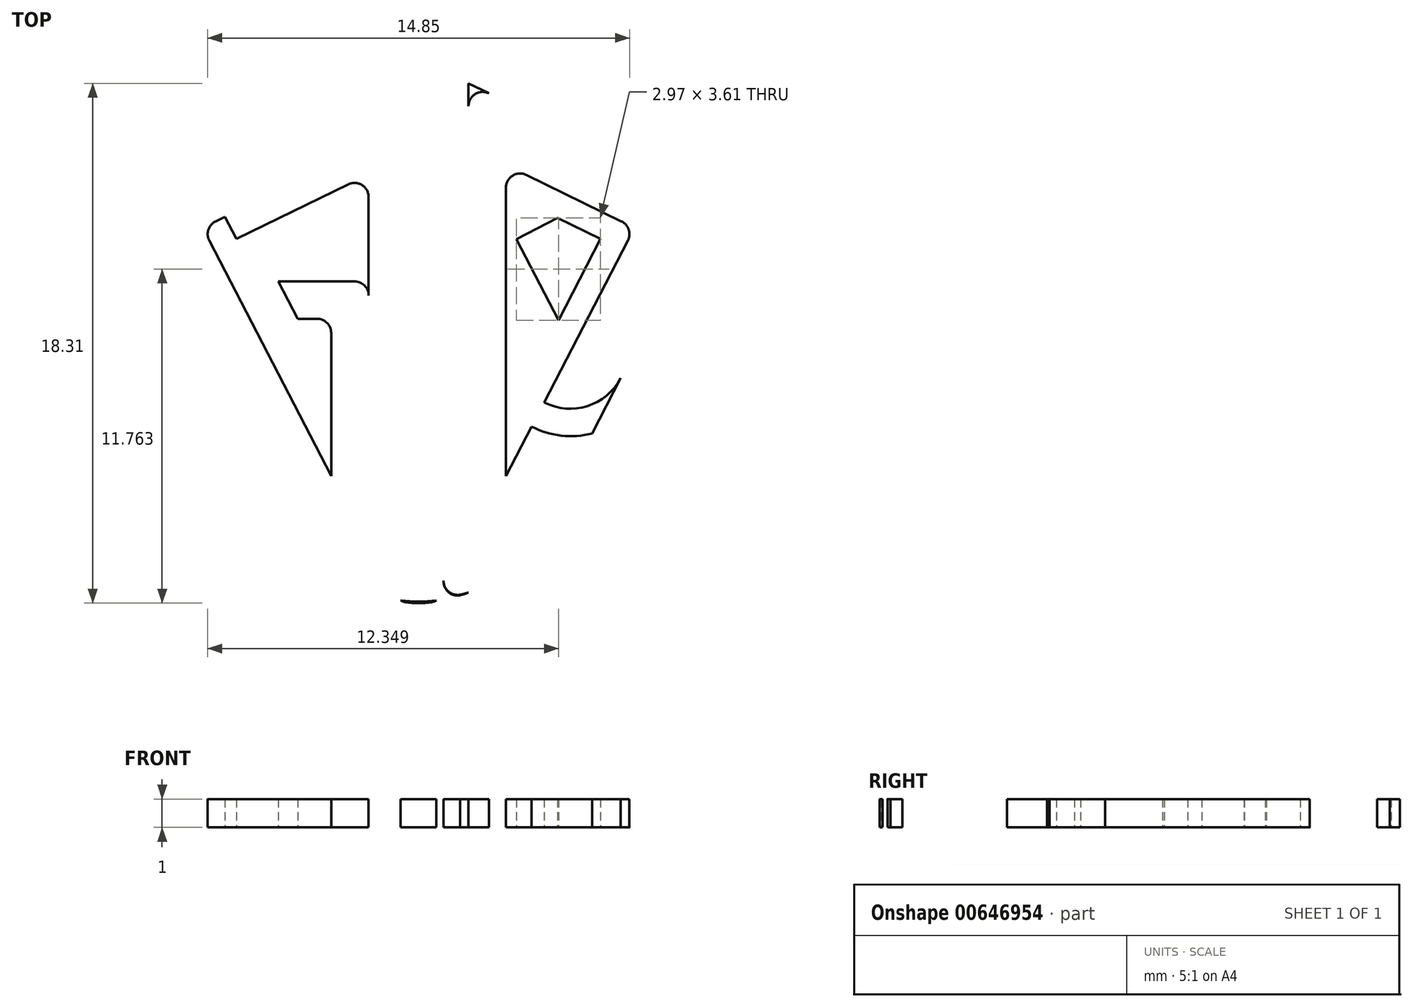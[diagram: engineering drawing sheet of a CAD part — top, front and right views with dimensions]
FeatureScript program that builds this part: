
annotation { "Feature Type Name" : "Feature", "Feature Type Description" : "" }
export const myFeature = defineFeature(function(context is Context, id is Id, definition is map)
    precondition{}
    {
        {
            var Q0;
            Q0=qCreatedBy(makeId("Top.planeOp"),FACE);
            var sketch = newSketch(context, id + "F0", { "sketchPlane" : qUnion([Q0])});
            skArc(sketch, "E0.MirrorCS", {"start": v(-12.62, 8.93) * mm, "mid": v(-12.18, 9.03) * mm, "end": v(-11.74, 8.93) * mm});
            skArc(sketch, "E1.MirrorCS", {"start": v(-1.42, 3.88) * mm, "mid": v(-0.9, 3.3) * mm, "end": v(-0.97, 2.52) * mm});
            skArc(sketch, "E2.MirrorCS", {"start": v(-23.38, 2.52) * mm, "mid": v(-23.45, 3.3) * mm, "end": v(-22.94, 3.88) * mm});
            skPoint(sketch, "E3.MirrorP", {"position": v(-23.85, 3.43) * mm});
            skArc(sketch, "E4.MirrorCS", {"start": v(-6.85, -8.84) * mm, "mid": v(-12.18, -12.09) * mm, "end": v(-17.5, -8.84) * mm});
            skLineSegment(sketch, "E5.MirrorCS", {"start": v(-4.15, -3.64) * mm, "end": v(-0.97, 2.52) * mm});
            skLineSegment(sketch, "E6.MirrorCS", {"start": v(-12.62, 8.93) * mm, "end": v(-22.94, 3.88) * mm});
            skLineSegment(sketch, "E7.MirrorCS", {"start": v(-23.38, 2.52) * mm, "end": v(-17.5, -8.84) * mm});
            skLineSegment(sketch, "E8.MirrorCS", {"start": v(-1.42, 3.88) * mm, "end": v(-11.74, 8.93) * mm});
            skLineSegment(sketch, "E9", {"start": v(-22.26, 2.53) * mm, "end": v(-16.62, -8.38) * mm});
            skArc(sketch, "E10.filletArc", {"start": v(-9.67, -10.41) * mm, "mid": v(-8.56, -9.53) * mm, "end": v(-7.74, -8.38) * mm});
            skLineSegment(sketch, "E11.MirrorCS", {"start": v(-10.42, 3.03) * mm, "end": v(-10.42, 0.52) * mm});
            skLineSegment(sketch, "E12.bottom", {"start": v(-15.25, 0.2) * mm, "end": v(-16.07, 0.2) * mm});
            skLineSegment(sketch, "E12.top", {"start": v(-15.75, -1.12) * mm, "end": v(-16.07, -1.12) * mm});
            skLineSegment(sketch, "E13", {"start": v(-15.25, 0.2) * mm, "end": v(-14.44, 0.2) * mm});
            skPoint(sketch, "E14", {"position": v(-16.57, -8.47) * mm});
            skPoint(sketch, "E15", {"position": v(-15.25, -10.03) * mm});
            skPoint(sketch, "E16", {"position": v(-13.94, -10.77) * mm});
            skPoint(sketch, "E17", {"position": v(-13.06, -11) * mm});
            skPoint(sketch, "E18", {"position": v(-11.3, -11) * mm});
            skPoint(sketch, "E19", {"position": v(-10.42, -10.77) * mm});
            skPoint(sketch, "E20", {"position": v(-9.1, -10.03) * mm});
            skPoint(sketch, "E21", {"position": v(-9.1, -6.67) * mm});
            skPoint(sketch, "E22", {"position": v(-2.78, 1.2) * mm});
            skPoint(sketch, "E23", {"position": v(-4.57, 2.08) * mm});
            skPoint(sketch, "E24", {"position": v(-9.1, 6.52) * mm});
            skPoint(sketch, "E25", {"position": v(-10.42, 7.17) * mm});
            skPoint(sketch, "E26", {"position": v(-11.3, 7.6) * mm});
            skPoint(sketch, "E27", {"position": v(-13.06, 7.6) * mm});
            skPoint(sketch, "E28", {"position": v(-13.94, 7.17) * mm});
            skPoint(sketch, "E29", {"position": v(-15.25, 4.3) * mm});
            skPoint(sketch, "E30", {"position": v(-13.94, 4.94) * mm});
            skPoint(sketch, "E31", {"position": v(-13.06, 5.37) * mm});
            skPoint(sketch, "E32", {"position": v(-10.42, 4.94) * mm});
            skPoint(sketch, "E33", {"position": v(-21.58, 1.2) * mm});
            skPoint(sketch, "E34", {"position": v(-19.78, 2.08) * mm});
            skPoint(sketch, "E35", {"position": v(-16.57, -4.12) * mm});
            skPoint(sketch, "E36", {"position": v(-16.57, -1.12) * mm});
            skPoint(sketch, "E37", {"position": v(-16.57, 0.2) * mm});
            skPoint(sketch, "E38", {"position": v(-15.25, 0.2) * mm});
            skPoint(sketch, "E39", {"position": v(-15.25, -1.12) * mm});
            skPoint(sketch, "E40", {"position": v(-13.94, 0.2) * mm});
            skLineSegment(sketch, "E41", {"start": v(-2.78, 1.2) * mm, "end": v(-2.1, 2.53) * mm});
            skLineSegment(sketch, "E42", {"start": v(-3.82, 3.94) * mm, "end": v(-6.39, 5.2) * mm});
            skLineSegment(sketch, "E43", {"start": v(-6.4, -1.43) * mm, "end": v(-4.8, 1.63) * mm});
            skLineSegment(sketch, "E44", {"start": v(-5.03, 2.3) * mm, "end": v(-6.4, 2.97) * mm});
            skLineSegment(sketch, "E45", {"start": v(-9.1, 3.5) * mm, "end": v(-9.1, -6.67) * mm});
            skLineSegment(sketch, "E46", {"start": v(-22.04, 3.2) * mm, "end": v(-14.65, 6.82) * mm});
            skLineSegment(sketch, "E47", {"start": v(-12.78, 7.74) * mm, "end": v(-12.4, 7.92) * mm});
            skLineSegment(sketch, "E48", {"start": v(-11.96, 7.92) * mm, "end": v(-11.58, 7.74) * mm});
            skLineSegment(sketch, "E49", {"start": v(-15.25, 4.3) * mm, "end": v(-19.32, 2.3) * mm});
            skLineSegment(sketch, "E50", {"start": v(-19.55, 1.63) * mm, "end": v(-16.57, -4.12) * mm});
            skLineSegment(sketch, "E51", {"start": v(-15.25, -1.62) * mm, "end": v(-15.25, -10.03) * mm});
            skPoint(sketch, "E52", {"position": v(-15.25, -6.67) * mm});
            skLineSegment(sketch, "E53", {"start": v(-16.57, -4.12) * mm, "end": v(-15.25, -6.67) * mm});
            skLineSegment(sketch, "E54", {"start": v(-15.25, 4.3) * mm, "end": v(-14.65, 4.59) * mm});
            skLineSegment(sketch, "E55", {"start": v(-9.1, 6.52) * mm, "end": v(-9.7, 6.82) * mm});
            skArc(sketch, "E56.filletArc", {"start": v(-22.04, 3.2) * mm, "mid": v(-22.3, 2.91) * mm, "end": v(-22.26, 2.53) * mm});
            skArc(sketch, "E57.filletArc", {"start": v(-2.1, 2.53) * mm, "mid": v(-2.06, 2.91) * mm, "end": v(-2.32, 3.2) * mm});
            skArc(sketch, "E58.filletArc", {"start": v(-13.94, 6.37) * mm, "mid": v(-14.17, 6.8) * mm, "end": v(-14.65, 6.82) * mm});
            skArc(sketch, "E59.filletArc", {"start": v(-9.7, 6.82) * mm, "mid": v(-10.18, 6.8) * mm, "end": v(-10.42, 6.37) * mm});
            skArc(sketch, "E60.filletArc", {"start": v(-8.38, 3.94) * mm, "mid": v(-8.87, 3.92) * mm, "end": v(-9.1, 3.5) * mm});
            skArc(sketch, "E61.filletArc", {"start": v(-4.8, 1.63) * mm, "mid": v(-4.78, 2.01) * mm, "end": v(-5.03, 2.3) * mm});
            skArc(sketch, "E62.filletArc", {"start": v(-19.32, 2.3) * mm, "mid": v(-19.58, 2.01) * mm, "end": v(-19.55, 1.63) * mm});
            skArc(sketch, "E63.filletArc", {"start": v(-13.94, 4.14) * mm, "mid": v(-14.17, 4.56) * mm, "end": v(-14.65, 4.59) * mm});
            skArc(sketch, "E64.filletArc", {"start": v(-15.25, -1.62) * mm, "mid": v(-15.4, -1.27) * mm, "end": v(-15.75, -1.12) * mm});
            skArc(sketch, "E65.filletArc", {"start": v(-13.94, -0.3) * mm, "mid": v(-14.08, 0.05) * mm, "end": v(-14.44, 0.2) * mm});
            skLineSegment(sketch, "E66", {"start": v(-13.94, 4.14) * mm, "end": v(-13.94, 6.37) * mm});
            skArc(sketch, "E67.filletArc", {"start": v(-11.96, 7.92) * mm, "mid": v(-12.18, 7.97) * mm, "end": v(-12.4, 7.92) * mm});
            skArc(sketch, "E68.filletArc", {"start": v(-12.78, 7.74) * mm, "mid": v(-12.98, 7.55) * mm, "end": v(-13.06, 7.29) * mm});
            skArc(sketch, "E69.filletArc", {"start": v(-11.3, 7.29) * mm, "mid": v(-11.37, 7.55) * mm, "end": v(-11.58, 7.74) * mm});
            skArc(sketch, "E70.filletArc", {"start": v(-10.42, -9.98) * mm, "mid": v(-10.17, -10.41) * mm, "end": v(-9.67, -10.41) * mm});
            skArc(sketch, "E71.MirrorCS", {"start": v(-14.69, -10.41) * mm, "mid": v(-15.8, -9.53) * mm, "end": v(-16.62, -8.38) * mm});
            skArc(sketch, "E72.MirrorCS", {"start": v(-13.94, -9.98) * mm, "mid": v(-14.19, -10.41) * mm, "end": v(-14.69, -10.41) * mm});
            skArc(sketch, "E73", {"start": v(-12.63, -11.1) * mm, "mid": v(-12.18, -11.14) * mm, "end": v(-11.72, -11.1) * mm});
            skLineSegment(sketch, "E74", {"start": v(-13.94, -9.98) * mm, "end": v(-13.94, -0.3) * mm});
            skLineSegment(sketch, "E75", {"start": v(-13.06, -10.37) * mm, "end": v(-13.06, 6.8) * mm});
            skLineSegment(sketch, "E76", {"start": v(-11.3, 7.29) * mm, "end": v(-11.3, -10.35) * mm});
            skArc(sketch, "E77.filletArc", {"start": v(-13.06, -10.61) * mm, "mid": v(-12.94, -10.94) * mm, "end": v(-12.63, -11.1) * mm});
            skArc(sketch, "E78.filletArc", {"start": v(-11.72, -11.1) * mm, "mid": v(-11.42, -10.94) * mm, "end": v(-11.3, -10.61) * mm});
            skLineSegment(sketch, "E79", {"start": v(-16.07, 0.2) * mm, "end": v(-17.12, 0.2) * mm});
            skLineSegment(sketch, "E80", {"start": v(-16.07, -1.12) * mm, "end": v(-16.57, -1.12) * mm});
            skPoint(sketch, "E81", {"position": v(-16.43, -1.12) * mm});
            skLineSegment(sketch, "E82", {"start": v(-16.43, -1.12) * mm, "end": v(-17.12, 0.2) * mm});
            skPoint(sketch, "E83", {"position": v(-6.84, 2.08) * mm});
            skPoint(sketch, "E84", {"position": v(-6.84, 3.19) * mm});
            skPoint(sketch, "E85", {"position": v(-6.84, -2.3) * mm});
            skPoint(sketch, "E86", {"position": v(-9.1, 2.08) * mm});
            skLineSegment(sketch, "E87", {"start": v(-7.28, 2.97) * mm, "end": v(-8.64, 2.3) * mm});
            skLineSegment(sketch, "E88", {"start": v(-8.87, 1.63) * mm, "end": v(-7.28, -1.43) * mm});
            skPoint(sketch, "E89", {"position": v(-6.83, 5.4) * mm});
            skPoint(sketch, "E90", {"position": v(-5.42, 0.45) * mm});
            skPoint(sketch, "E91", {"position": v(-10.42, 3.65) * mm});
            skLineSegment(sketch, "E92", {"start": v(-9.86, 3.93) * mm, "end": v(-7.27, 5.2) * mm});
            skPoint(sketch, "E93", {"position": v(-7.96, -4.47) * mm});
            skPoint(sketch, "E94", {"position": v(-10.42, 0.28) * mm});
            skPoint(sketch, "E95", {"position": v(-9.1, -2.27) * mm});
            skLineSegment(sketch, "E96", {"start": v(-6.84, 3.19) * mm, "end": v(-6.84, 2.08) * mm});
            skPoint(sketch, "E97", {"position": v(-3.26, 0.28) * mm});
            skPoint(sketch, "E98", {"position": v(-3.26, 3.66) * mm});
            skLineSegment(sketch, "E99", {"start": v(-3.26, 3.04) * mm, "end": v(-3.26, 0.52) * mm});
            skLineSegment(sketch, "E100", {"start": v(-12.18, -6.09) * mm, "end": v(-12.18, -8.2) * mm});
            skLineSegment(sketch, "E101.MirrorCS", {"start": v(-21.1, 3.66) * mm, "end": v(-21.1, 0.28) * mm});
            skLineSegment(sketch, "E102.MirrorCS", {"start": v(-4.57, 2.08) * mm, "end": v(-6.84, -2.3) * mm});
            skLineSegment(sketch, "E103.MirrorCS", {"start": v(-6.84, 3.19) * mm, "end": v(-4.57, 2.08) * mm});
            skPoint(sketch, "E104", {"position": v(-11.3, 5.38) * mm});
            skPoint(sketch, "E105", {"position": v(-11.3, -10.04) * mm});
            skPoint(sketch, "E106", {"position": v(-13.06, -10.04) * mm});
            skPoint(sketch, "E107", {"position": v(-12.17, 5.8) * mm});
            skPoint(sketch, "E108", {"position": v(-13.06, -6.65) * mm});
            skPoint(sketch, "E109", {"position": v(-11.3, -6.65) * mm});
            skLineSegment(sketch, "E110", {"start": v(-13.94, 7.17) * mm, "end": v(-13.78, 7.25) * mm});
            skLineSegment(sketch, "E111", {"start": v(-13.06, 5.37) * mm, "end": v(-13.06, 7.6) * mm});
            skArc(sketch, "E112.filletArc", {"start": v(-13.06, 6.8) * mm, "mid": v(-13.3, 7.22) * mm, "end": v(-13.78, 7.25) * mm});
            skLineSegment(sketch, "E113", {"start": v(-13.94, 7.17) * mm, "end": v(-12.78, 7.74) * mm});
            skLineSegment(sketch, "E114", {"start": v(-11.3, -10.04) * mm, "end": v(-11.3, -11) * mm});
            skLineSegment(sketch, "E115", {"start": v(-10.42, -10.77) * mm, "end": v(-10.67, -10.83) * mm});
            skArc(sketch, "E116.filletArc", {"start": v(-11.3, -10.35) * mm, "mid": v(-11.1, -10.75) * mm, "end": v(-10.67, -10.83) * mm});
            skLineSegment(sketch, "E117", {"start": v(-13.06, -10.04) * mm, "end": v(-13.06, -11) * mm});
            skLineSegment(sketch, "E118", {"start": v(-14.06, -10.77) * mm, "end": v(-13.67, -10.86) * mm});
            skPoint(sketch, "E119.newPointA", {"position": v(-13.06, -10.61) * mm});
            skArc(sketch, "E119.filletArc", {"start": v(-13.67, -10.86) * mm, "mid": v(-13.25, -10.77) * mm, "end": v(-13.06, -10.37) * mm});
            skLineSegment(sketch, "E120", {"start": v(-21.58, 1.2) * mm, "end": v(-16.62, -8.38) * mm});
            skPoint(sketch, "E121", {"position": v(-12.18, -16.97) * mm});
            skArc(sketch, "E122.filletArc", {"start": v(-16.62, -8.38) * mm, "mid": v(-12.18, -11.09) * mm, "end": v(-7.74, -8.38) * mm});
            skArc(sketch, "E123.filletArc", {"start": v(-6.39, 5.2) * mm, "mid": v(-6.83, 5.3) * mm, "end": v(-7.27, 5.2) * mm});
            skArc(sketch, "E124.filletArc", {"start": v(-3.26, 3.04) * mm, "mid": v(-3.4, 3.57) * mm, "end": v(-3.82, 3.94) * mm});
            skArc(sketch, "E125.filletArc", {"start": v(-3.37, 0.06) * mm, "mid": v(-3.28, 0.28) * mm, "end": v(-3.26, 0.52) * mm});
            skArc(sketch, "E126.filletArc", {"start": v(-9.86, 3.93) * mm, "mid": v(-10.27, 3.56) * mm, "end": v(-10.42, 3.03) * mm});
            skArc(sketch, "E127.filletArc", {"start": v(-10.42, 0.52) * mm, "mid": v(-10.4, 0.28) * mm, "end": v(-10.3, 0.06) * mm});
            skArc(sketch, "E128.filletArc", {"start": v(-6.4, 2.97) * mm, "mid": v(-6.84, 3.08) * mm, "end": v(-7.28, 2.97) * mm});
            skArc(sketch, "E129.filletArc", {"start": v(-8.64, 2.3) * mm, "mid": v(-8.9, 2.01) * mm, "end": v(-8.87, 1.63) * mm});
            skLineSegment(sketch, "E130", {"start": v(-3.82, 3.94) * mm, "end": v(-11.3, 7.6) * mm});
            skLineSegment(sketch, "E131", {"start": v(-10.42, 0.52) * mm, "end": v(-10.42, 7.17) * mm});
            skLineSegment(sketch, "E132", {"start": v(-9.77, 4.95) * mm, "end": v(-7.83, 5.9) * mm});
            skLineSegment(sketch, "E133", {"start": v(-7.83, 5.9) * mm, "end": v(-9.77, 4.95) * mm});
            skLineSegment(sketch, "E134", {"start": v(-9.77, 4.95) * mm, "end": v(-10.42, 4.63) * mm});
            skPoint(sketch, "E135", {"position": v(-8.5, -3.42) * mm});
            skLineSegment(sketch, "E136", {"start": v(-16.9, 2.51) * mm, "end": v(-19.8, 1.1) * mm});
            skLineSegment(sketch, "E137", {"start": v(-19.8, 1.1) * mm, "end": v(-16.9, 2.51) * mm});
            skLineSegment(sketch, "E138", {"start": v(-16.9, 2.51) * mm, "end": v(-14.65, 3.61) * mm});
            skLineSegment(sketch, "E139", {"start": v(-19.12, 0.8) * mm, "end": v(-18.34, 1.21) * mm});
            skLineSegment(sketch, "E140", {"start": v(-18.34, 1.21) * mm, "end": v(-19.55, 3.55) * mm});
            skLineSegment(sketch, "E141", {"start": v(-19.55, 3.55) * mm, "end": v(-18.34, 1.21) * mm});
            skLineSegment(sketch, "E142", {"start": v(-19.55, 3.55) * mm, "end": v(-15.64, -4.01) * mm});
            skLineSegment(sketch, "E143", {"start": v(-16.13, -2.63) * mm, "end": v(-16.13, -3.81) * mm});
            skLineSegment(sketch, "E144", {"start": v(-16.13, -1.46) * mm, "end": v(-16.13, -3.81) * mm});
            skLineSegment(sketch, "E145", {"start": v(-13.94, 3.16) * mm, "end": v(-13.94, -0.3) * mm});
            skLineSegment(sketch, "E146", {"start": v(-15.25, 1.07) * mm, "end": v(-18.6, 1.07) * mm});
            skLineSegment(sketch, "E147", {"start": v(-18.6, 1.07) * mm, "end": v(-15.25, 1.07) * mm});
            skLineSegment(sketch, "E148", {"start": v(-13.7, 1.07) * mm, "end": v(-15.25, 1.07) * mm});
            skArc(sketch, "E149.filletArc", {"start": v(-13.94, 3.16) * mm, "mid": v(-14.17, 3.59) * mm, "end": v(-14.65, 3.61) * mm});
            skLineSegment(sketch, "E150", {"start": v(-2.38, 2.4) * mm, "end": v(-2.38, 1.75) * mm});
            skLineSegment(sketch, "E151", {"start": v(-2.38, 1.75) * mm, "end": v(-2.38, 3.6) * mm});
            skLineSegment(sketch, "E152", {"start": v(-3.82, 3.94) * mm, "end": v(-1.86, 2.98) * mm});
            skLineSegment(sketch, "E153", {"start": v(-16.07, -2) * mm, "end": v(-17.03, -2) * mm});
            skArc(sketch, "E154.filletArc", {"start": v(-7.28, -1.43) * mm, "mid": v(-6.84, -1.7) * mm, "end": v(-6.4, -1.43) * mm});
            skLineSegment(sketch, "E155", {"start": v(-7.74, -8.38) * mm, "end": v(-6.84, -6.65) * mm});
            skPoint(sketch, "E156", {"position": v(-7.9, 1.68) * mm});
            skPoint(sketch, "E157", {"position": v(-6.86, 2.22) * mm});
            skPoint(sketch, "E158", {"position": v(-5.77, 1.69) * mm});
            skPoint(sketch, "E159", {"position": v(-6.84, -0.38) * mm});
            skLineSegment(sketch, "E160", {"start": v(-7.9, 1.68) * mm, "end": v(-6.86, 2.22) * mm});
            skLineSegment(sketch, "E161", {"start": v(-6.86, 2.22) * mm, "end": v(-5.77, 1.69) * mm});
            skLineSegment(sketch, "E162", {"start": v(-5.77, 1.69) * mm, "end": v(-6.84, -0.38) * mm});
            skLineSegment(sketch, "E163", {"start": v(-6.84, -0.38) * mm, "end": v(-7.9, 1.68) * mm});
            skLineSegment(sketch, "E164.MirrorCS", {"start": v(-10.42, -9.98) * mm, "end": v(-10.42, -0.3) * mm});
            skPoint(sketch, "E165", {"position": v(-6.82, -8.79) * mm});
            skLineSegment(sketch, "E166", {"start": v(-6.85, -8.84) * mm, "end": v(-6.82, -8.79) * mm});
            skPoint(sketch, "E167", {"position": v(-6.84, -6.65) * mm});
            skLineSegment(sketch, "E168", {"start": v(-2.78, 1.2) * mm, "end": v(-5.06, -3.21) * mm});
            skLineSegment(sketch, "E169", {"start": v(-8.61, -3.21) * mm, "end": v(-10.42, 0.28) * mm});
            skLineSegment(sketch, "E170", {"start": v(-10.42, 0.52) * mm, "end": v(-10.42, -0.3) * mm});
            skArc(sketch, "E171.filletArc", {"start": v(-8.61, -3.21) * mm, "mid": v(-6.84, -4.3) * mm, "end": v(-5.06, -3.21) * mm});
            skPoint(sketch, "E172", {"position": v(-10.42, -1.83) * mm});
            skPoint(sketch, "E173", {"position": v(-9.1, -4.38) * mm});
            skLineSegment(sketch, "E174", {"start": v(-5.5, -4.07) * mm, "end": v(-5.06, -3.21) * mm});
            skLineSegment(sketch, "E175", {"start": v(-9.1, -2.27) * mm, "end": v(-8.17, -4.07) * mm});
            skPoint(sketch, "E176", {"position": v(-0.97, 2.52) * mm});
            skPoint(sketch, "E177", {"position": v(-4.15, -3.64) * mm});
            skLineSegment(sketch, "E178", {"start": v(-10.42, -1.83) * mm, "end": v(-9.48, -3.64) * mm});
            skArc(sketch, "E179.filletArc", {"start": v(-9.48, -3.64) * mm, "mid": v(-6.82, -5.26) * mm, "end": v(-4.15, -3.64) * mm});
            skLineSegment(sketch, "E180", {"start": v(-6.82, -8.79) * mm, "end": v(-4.15, -3.64) * mm});
            skLineSegment(sketch, "E181", {"start": v(-6.84, -6.65) * mm, "end": v(-3.26, 0.28) * mm});
            skArc(sketch, "E182.MirrorCS", {"start": v(-10.68, -10.86) * mm, "mid": v(-11.1, -10.77) * mm, "end": v(-11.3, -10.37) * mm});
            skArc(sketch, "E183.MirrorCS", {"start": v(-11.3, -10.61) * mm, "mid": v(-11.42, -10.94) * mm, "end": v(-11.72, -11.1) * mm});
            skArc(sketch, "E184.MirrorCS", {"start": v(-7.74, -8.38) * mm, "mid": v(-12.18, -11.09) * mm, "end": v(-16.62, -8.38) * mm});
            skLineSegment(sketch, "E185.MirrorCS", {"start": v(-4.8, 1.63) * mm, "end": v(-7.78, -4.12) * mm});
            skLineSegment(sketch, "E186.MirrorCS", {"start": v(-9.1, -1.62) * mm, "end": v(-9.1, -10.03) * mm});
            skLineSegment(sketch, "E187.MirrorCS", {"start": v(-9.1, 4.3) * mm, "end": v(-5.03, 2.3) * mm});
            skArc(sketch, "E188.MirrorCS", {"start": v(-5.03, 2.3) * mm, "mid": v(-4.78, 2.01) * mm, "end": v(-4.8, 1.63) * mm});
            skLineSegment(sketch, "E189.MirrorCS", {"start": v(-7.78, -4.12) * mm, "end": v(-9.1, -6.67) * mm});
            skLineSegment(sketch, "E190", {"start": v(-5.77, 1.69) * mm, "end": v(-4.78, 1.69) * mm});
            skLineSegment(sketch, "E191", {"start": v(-7.9, 1.68) * mm, "end": v(-9.1, 1.68) * mm});
            skLineSegment(sketch, "E192", {"start": v(-9.1, 1.68) * mm, "end": v(-8.11, 1.68) * mm});
            skLineSegment(sketch, "E193", {"start": v(-8.11, 1.68) * mm, "end": v(-9.1, 1.68) * mm});
            skPoint(sketch, "E194", {"position": v(-8.11, 1.68) * mm});
            skLineSegment(sketch, "E195", {"start": v(-8.11, 1.68) * mm, "end": v(-6.61, 2.46) * mm});
            skLineSegment(sketch, "E196", {"start": v(-5.77, 1.69) * mm, "end": v(-7.06, 2.32) * mm});
            skPoint(sketch, "E197", {"position": v(-6.97, 2.27) * mm});
            skLineSegment(sketch, "E198", {"start": v(-8.11, 1.68) * mm, "end": v(-6.76, -0.93) * mm});
            skLineSegment(sketch, "E199", {"start": v(-5.77, 1.69) * mm, "end": v(-7.05, -0.78) * mm});
            skPoint(sketch, "E200", {"position": v(-6.94, -0.58) * mm});
            skLineSegment(sketch, "E201.MirrorCS", {"start": v(-7.17, -0.55) * mm, "end": v(-8.23, 1.51) * mm});
            skLineSegment(sketch, "E202.MirrorCS", {"start": v(-8, 1.85) * mm, "end": v(-6.95, 2.4) * mm});
            skLineSegment(sketch, "E203", {"start": v(-8, 1.85) * mm, "end": v(-8.6, 1.55) * mm});
            skLineSegment(sketch, "E204", {"start": v(-8.23, 1.51) * mm, "end": v(-8.46, 1.98) * mm});
            skLineSegment(sketch, "E205", {"start": v(-7.17, -0.55) * mm, "end": v(-6.89, -1.08) * mm});
            skLineSegment(sketch, "E206", {"start": v(-7.06, 2.32) * mm, "end": v(-7.16, 2.37) * mm});
            skLineSegment(sketch, "E207.MirrorCS", {"start": v(-8.2, 1.85) * mm, "end": v(-6.7, 2.62) * mm});
            skLineSegment(sketch, "E208.MirrorCS", {"start": v(-8.08, 2.02) * mm, "end": v(-7.03, 2.56) * mm});
            skLineSegment(sketch, "E209.MirrorCS", {"start": v(-8.44, 1.51) * mm, "end": v(-7.09, -1.1) * mm});
            skLineSegment(sketch, "E210.MirrorCS", {"start": v(-7.5, -0.72) * mm, "end": v(-8.56, 1.34) * mm});
            skLineSegment(sketch, "E211", {"start": v(-6.84, -0.38) * mm, "end": v(-7.28, -1.24) * mm});
            skLineSegment(sketch, "E212", {"start": v(-7.5, -0.72) * mm, "end": v(-7.18, -1.33) * mm});
            skLineSegment(sketch, "E213", {"start": v(-8.2, 1.85) * mm, "end": v(-8.7, 1.6) * mm});
            skLineSegment(sketch, "E214", {"start": v(-8.08, 2.02) * mm, "end": v(-8.8, 1.65) * mm});
            skLineSegment(sketch, "E215", {"start": v(-8.56, 1.34) * mm, "end": v(-8.77, 1.75) * mm});
            skLineSegment(sketch, "E216", {"start": v(-8.44, 1.51) * mm, "end": v(-8.6, 1.85) * mm});
            skPoint(sketch, "E216.endSnap0", {"position": v(-8.6, 1.68) * mm});
            skLineSegment(sketch, "E217", {"start": v(-8.6, 1.55) * mm, "end": v(-8.72, 1.49) * mm});
            skLineSegment(sketch, "E218", {"start": v(-7.16, 2.37) * mm, "end": v(-7.76, 2.66) * mm});
            skLineSegment(sketch, "E219.MirrorCS", {"start": v(-2.78, 1.2) * mm, "end": v(-7.74, -8.38) * mm});
            skLineSegment(sketch, "E220.MirrorCS", {"start": v(-0.97, 2.52) * mm, "end": v(-6.85, -8.84) * mm});
            skPoint(sketch, "E221.newPointA", {"position": v(-10.7, -19.84) * mm});
            skPoint(sketch, "E221.newPointB", {"position": v(-13.66, -19.84) * mm});
            skPoint(sketch, "E222.newPointA", {"position": v(-10.27, -22.82) * mm});
            skPoint(sketch, "E222.newPointB", {"position": v(-14.08, -22.82) * mm});
            skArc(sketch, "E222.filletArc", {"start": v(-17.5, -8.84) * mm, "mid": v(-12.18, -12.09) * mm, "end": v(-6.85, -8.84) * mm});
            skSolve(sketch);
        }
        {
            var Q0;
            {var subQ4=sQuery(id+"F0.wireOp",EDGE,"E138");Q0=makeQuery(id+"F0.imprint","IMPRINT",FACE,{"disambiguationData":[TD([[makeQuery(id+"F0.imprint","IMPRINT",EDGE,{"derivedFrom":subQ4}),-1.0]])]});}
            var Q1;
            Q1=makeQuery(id+"F0.imprint","IMPRINT",FACE,{"disambiguationData":[TD([[makeQuery(id+"F0.imprint","IMPRINT",EDGE,{"derivedFrom":sQuery(id+"F0.wireOp",EDGE,"E12.bottom")}),-1.0]])]});
            var Q2;
            {var subQ0=sQuery(id+"F0.wireOp",EDGE,"E144");var subQ5=makeQuery(id+"F0.imprint","IMPRINT",VERTEX,{"derivedFrom":subQ0});Q2=makeQuery(id+"F0.imprint","IMPRINT",FACE,{"disambiguationData":[TD([[makeQuery(id+"F0.imprint","IMPRINT",EDGE,{"disambiguationData":[TD([[subQ5,1.0]])],"derivedFrom":subQ0}),-1.0]])]});}
            var Q3;
            {var subQ0=sQuery(id+"F0.wireOp",EDGE,"E62.filletArc");Q3=makeQuery(id+"F0.imprint","IMPRINT",FACE,{"disambiguationData":[TD([[makeQuery(id+"F0.imprint","IMPRINT",EDGE,{"derivedFrom":subQ0}),1.0]])]});}
            var Q4;
            {var subQ1=sQuery(id+"F0.wireOp",EDGE,"E139");var subQ4=sQuery(id+"F0.wireOp",EDGE,"E50");var subQ5=makeQuery(id+"F0.imprint","INTERSECT",VERTEX,{"derivedFrom":[subQ4,subQ1]});Q4=makeQuery(id+"F0.imprint","IMPRINT",FACE,{"disambiguationData":[TD([[makeQuery(id+"F0.imprint","IMPRINT",EDGE,{"disambiguationData":[TD([[subQ5,1.0]])],"derivedFrom":subQ4}),1.0]])]});}
            var Q5;
            {var subQ0=sQuery(id+"F0.wireOp",EDGE,"E142");var subQ1=sQuery(id+"F0.wireOp",EDGE,"E139");var subQ2=makeQuery(id+"F0.imprint","INTERSECT",VERTEX,{"derivedFrom":[subQ1,subQ0]});Q5=makeQuery(id+"F0.imprint","IMPRINT",FACE,{"disambiguationData":[TD([[makeQuery(id+"F0.imprint","IMPRINT",EDGE,{"disambiguationData":[TD([[subQ2,1.0]])],"derivedFrom":subQ1}),-1.0]])]});}
            var Q6;
            {var subQ0=sQuery(id+"F0.wireOp",EDGE,"ozTpNQaU-grU3-HA9w-UyX2-o1CqBorec6r5");Q6=makeQuery(id+"F0.imprint","IMPRINT",FACE,{"disambiguationData":[TD([[makeQuery(id+"F0.imprint","IMPRINT",EDGE,{"derivedFrom":subQ0}),-1.0]])]});}
            var Q7;
            {var subQ2=sQuery(id+"F0.wireOp",EDGE,"3e2ccfe4-6b2a-43d4-8b51-7597902346a8.filletArc");Q7=makeQuery(id+"F0.imprint","IMPRINT",FACE,{"disambiguationData":[TD([[makeQuery(id+"F0.imprint","IMPRINT",EDGE,{"derivedFrom":subQ2}),-1.0]])]});}
            var Q8;
            {var subQ7=sQuery(id+"F0.wireOp",EDGE,"E61.filletArc");Q8=makeQuery(id+"F0.imprint","IMPRINT",FACE,{"disambiguationData":[TD([[makeQuery(id+"F0.imprint","IMPRINT",EDGE,{"derivedFrom":subQ7}),1.0]])]});}
            var Q9;
            {var subQ8=sQuery(id+"F0.wireOp",EDGE,"Ewz0VHGi-sKfj-zBBT-7Waf-a84nxzi6t6Pn");Q9=makeQuery(id+"F0.imprint","IMPRINT",FACE,{"disambiguationData":[TD([[makeQuery(id+"F0.imprint","IMPRINT",EDGE,{"derivedFrom":subQ8}),1.0]])]});}
            var Q10;
            {var subQ0=sQuery(id+"F0.wireOp",EDGE,"E59.filletArc");Q10=makeQuery(id+"F0.imprint","IMPRINT",FACE,{"disambiguationData":[TD([[makeQuery(id+"F0.imprint","IMPRINT",EDGE,{"derivedFrom":subQ0}),-1.0]])]});}
            var Q11;
            {var subQ2=sQuery(id+"F0.wireOp",EDGE,"E115");Q11=makeQuery(id+"F0.imprint","IMPRINT",FACE,{"disambiguationData":[TD([[makeQuery(id+"F0.imprint","IMPRINT",EDGE,{"derivedFrom":subQ2}),1.0]])]});}
            var Q12;
            {var subQ0=sQuery(id+"F0.wireOp",EDGE,"E73");Q12=makeQuery(id+"F0.imprint","IMPRINT",FACE,{"disambiguationData":[TD([[makeQuery(id+"F0.imprint","IMPRINT",EDGE,{"derivedFrom":subQ0}),1.0]])]});}
            var Q13;
            Q13=makeQuery(id+"F0.imprint","IMPRINT",FACE,{"disambiguationData":[TD([[makeQuery(id+"F0.imprint","IMPRINT",EDGE,{"derivedFrom":sQuery(id+"F0.wireOp",EDGE,"E0.MirrorCS")}),-1.0]])]});
            var Q14;
            {var subQ3=sQuery(id+"F0.wireOp",EDGE,"E171.filletArc");var subQ9=sQuery(id+"F0.wireOp",EDGE,"E175");var subQ11=makeQuery(id+"F0.imprint","INTERSECT",VERTEX,{"derivedFrom":[subQ3,subQ9]});Q14=makeQuery(id+"F0.imprint","IMPRINT",FACE,{"disambiguationData":[TD([[makeQuery(id+"F0.imprint","IMPRINT",EDGE,{"disambiguationData":[TD([[subQ11,-1.0]])],"derivedFrom":subQ3}),-1.0]])]});}
            var Q15;
            {var subQ0=sQuery(id+"F0.wireOp",EDGE,"E186.MirrorCS");var subQ1=sQuery(id+"F0.wireOp",EDGE,"E179.filletArc");var subQ2=makeQuery(id+"F0.imprint","INTERSECT",VERTEX,{"derivedFrom":[subQ1,subQ0]});Q15=makeQuery(id+"F0.imprint","IMPRINT",FACE,{"disambiguationData":[TD([[makeQuery(id+"F0.imprint","IMPRINT",EDGE,{"disambiguationData":[TD([[subQ2,-1.0]])],"derivedFrom":subQ1}),-1.0]])]});}
            var Q16;
            {var subQ17=sQuery(id+"F0.wireOp",EDGE,"E88");Q16=makeQuery(id+"F0.imprint","IMPRINT",FACE,{"disambiguationData":[TD([[makeQuery(id+"F0.imprint","IMPRINT",EDGE,{"derivedFrom":subQ17}),1.0]])]});}
            var Q17;
            {var subQ0=sQuery(id+"F0.wireOp",EDGE,"E96");var subQ8=makeQuery(id+"F0.imprint","INTERSECT",VERTEX,{"derivedFrom":[subQ0,sQuery(id+"F0.wireOp",EDGE,"E207.MirrorCS")]});Q17=makeQuery(id+"F0.imprint","IMPRINT",FACE,{"disambiguationData":[TD([[makeQuery(id+"F0.imprint","IMPRINT",EDGE,{"disambiguationData":[TD([[subQ8,1.0]])],"derivedFrom":subQ0}),1.0]])]});}
            var Q18;
            {var subQ8=sQuery(id+"F0.wireOp",EDGE,"E87");Q18=makeQuery(id+"F0.imprint","IMPRINT",FACE,{"disambiguationData":[TD([[makeQuery(id+"F0.imprint","IMPRINT",EDGE,{"derivedFrom":subQ8}),1.0]])]});}
            var Q19;
            {var subQ6=sQuery(id+"F0.wireOp",EDGE,"E96");var subQ8=sQuery(id+"F0.wireOp",EDGE,"E207.MirrorCS");var subQ9=makeQuery(id+"F0.imprint","INTERSECT",VERTEX,{"derivedFrom":[subQ6,subQ8]});Q19=makeQuery(id+"F0.imprint","IMPRINT",FACE,{"disambiguationData":[TD([[makeQuery(id+"F0.imprint","IMPRINT",EDGE,{"disambiguationData":[TD([[subQ9,-1.0]])],"derivedFrom":subQ6}),-1.0]])]});}
            var Q20;
            {var subQ0=sQuery(id+"F0.wireOp",EDGE,"E195");var subQ1=sQuery(id+"F0.wireOp",EDGE,"E96");var subQ2=makeQuery(id+"F0.imprint","INTERSECT",VERTEX,{"derivedFrom":[subQ1,subQ0]});Q20=makeQuery(id+"F0.imprint","IMPRINT",FACE,{"disambiguationData":[TD([[makeQuery(id+"F0.imprint","IMPRINT",EDGE,{"disambiguationData":[TD([[subQ2,-1.0]])],"derivedFrom":subQ1}),-1.0]])]});}
            var Q21;
            {var subQ1=sQuery(id+"F0.wireOp",EDGE,"E88");Q21=makeQuery(id+"F0.imprint","IMPRINT",FACE,{"disambiguationData":[TD([[makeQuery(id+"F0.imprint","IMPRINT",EDGE,{"derivedFrom":subQ1}),-1.0]])]});}
            var Q22;
            {var subQ6=sQuery(id+"F0.wireOp",EDGE,"E60.filletArc");Q22=makeQuery(id+"F0.imprint","IMPRINT",FACE,{"disambiguationData":[TD([[makeQuery(id+"F0.imprint","IMPRINT",EDGE,{"derivedFrom":subQ6}),1.0]])]});}
            var Q23;
            {var subQ0=sQuery(id+"F0.wireOp",EDGE,"E187.MirrorCS");var subQ1=sQuery(id+"F0.wireOp",EDGE,"E96");var subQ2=makeQuery(id+"F0.imprint","INTERSECT",VERTEX,{"derivedFrom":[subQ1,subQ0]});Q23=makeQuery(id+"F0.imprint","IMPRINT",FACE,{"disambiguationData":[TD([[makeQuery(id+"F0.imprint","IMPRINT",EDGE,{"disambiguationData":[TD([[subQ2,-1.0]])],"derivedFrom":subQ1}),1.0]])]});}
            extrude(context, id + "F1", {"entities" : qUnion([Q0, Q1, Q2, Q3, Q4, Q5, Q6, Q7, Q8, Q9, Q10, Q11, Q12, Q13, Q14, Q15, Q16, Q17, Q18, Q19, Q20, Q21, Q22, Q23]), "depth" : 1 * mm, "offsetDistance" : 25 * mm});
        }
    });
